# Revit family: Accessory-Flush_Actuator_Plate-KOHLER-Droplet-K-4177
name_source: partatom
category: Specialty Equipment
revit_build: Autodesk Revit 2015 (Build: 20140606_1530(x64)
units: mm (PartAtom-declared; Revit-internal decimal feet)

## types (4) — shared parameters
ADA Compliant = No
Assembly Code = C1030200
Date Modified = 11/22/2018
Default Elevation = 42"
Description = Flush actuator plate for 2inch x 4inch in-wall tank and carrier system
Height = 6 5/16"
Length = 8 7/8"
Manufacturer = KOHLER Co.
MasterFormat 1995 = 10820
MasterFormat 2004 = 10.28.13
Material = Premium Metal Construction
Product Documentation Link = http://www.us.kohler.com
Product Name = Droplet
Product Page URL = http://www.us.kohler.com
URL = https://www.us.kohler.com
Width = 11/32"

## per-type parameters (varying)
| type | Finish | Model | Type |
| CP-Polished Chrome | Kohler-Metal-CP-Polished_Chrome | K-4177-CP | 1 |
| AF-Vibrant French Gold | Kohler-Metal-AF-Vibrant_French_Gold | K-4177-AF | 2 |
| BN-Vibrant Brushed Nickel | Kohler-Metal-BN-Vibrant_Brushed_Nickel | K-4177-BN | 3 |
| 7-Black Black | Kohler-Metal-7-Black_Black | K-4177-7 | 4 |

## geometry (parser evidence)
native form markers: Sweep x6
no freeform markers — native parametric forms only
